# Revit family: Lighting_Fixtures-Wall-Astro-Tangoxxx
name_source: partatom
category: Lighting Fixtures
revit_build: Autodesk Revit LT 2014 (Build: 20130308_1515(x64)
units: mm (PartAtom-declared; Revit-internal decimal feet)

## types (5) — shared parameters
Apparent Load = 2 VA
Assembly Code = D5020200
Class = 3
Color Filter = 16777215
Description = Wall light
Dimmable = If dimmable driver is used
Dimming Lamp Color Temperature Shift = <None>
Height = 70 mm  [stored 0.229659 ft]
IP Rating = IP65
Lamp = Dedicated LED
Lamp included = Yes
Length = 2 mm  [stored 0.00656168 ft]
Light Source From Wall = 50 mm  [stored 0.164042 ft]
Luminaire Lamp Efficiency Rating = A
Manufacturer = Astro Lighting Ltd, CM20 2DP
Mountable on normally flammable surfaces = Yes
Number of Poles = 1
Photometric Web File = 0825 TANGO WHITE.ies
Product Documentation = http://www.astrolighting.co.uk
Suitable for bathroom zone = Zones 1, 2 and 3
Tilt Angle = 90.00°
Type Comments = Wall box provided with fitting. Driver not included.
URL = www.astrolighting.co.uk
Voltage = 230 V
Wattage Comments = 1w
Weight = 0.2kg
Width = 70 mm  [stored 0.229659 ft]

## per-type parameters (varying)
| type | Casing Material | Model |
| 0825 Tango (White) | Astro - Aluminium - White | 0825 Tango White |
| 0831 Tango (Silver) | Astro - Aluminium - Silver Paint | 0831 Tango Silver |
| 0833 Tango (Polished Chrome) | Astro - Aluminium - Chrome Finish | 0833 Tango Polished Chrome |
| 0832 Tango (Black) | Astro - Aluminium - Black Paint | 0832 Tango Black |
| 0826 Tango (Stainless Steel) | Astro - Stainless Steel - Polished | 0826 Tango Stainless Steel |

note: [stored X ft] marks values corroborated as IEEE doubles in the binary element streams (Revit-internal decimal feet)

## geometry (parser evidence)
native form markers: Sweep x3
no freeform markers — native parametric forms only
